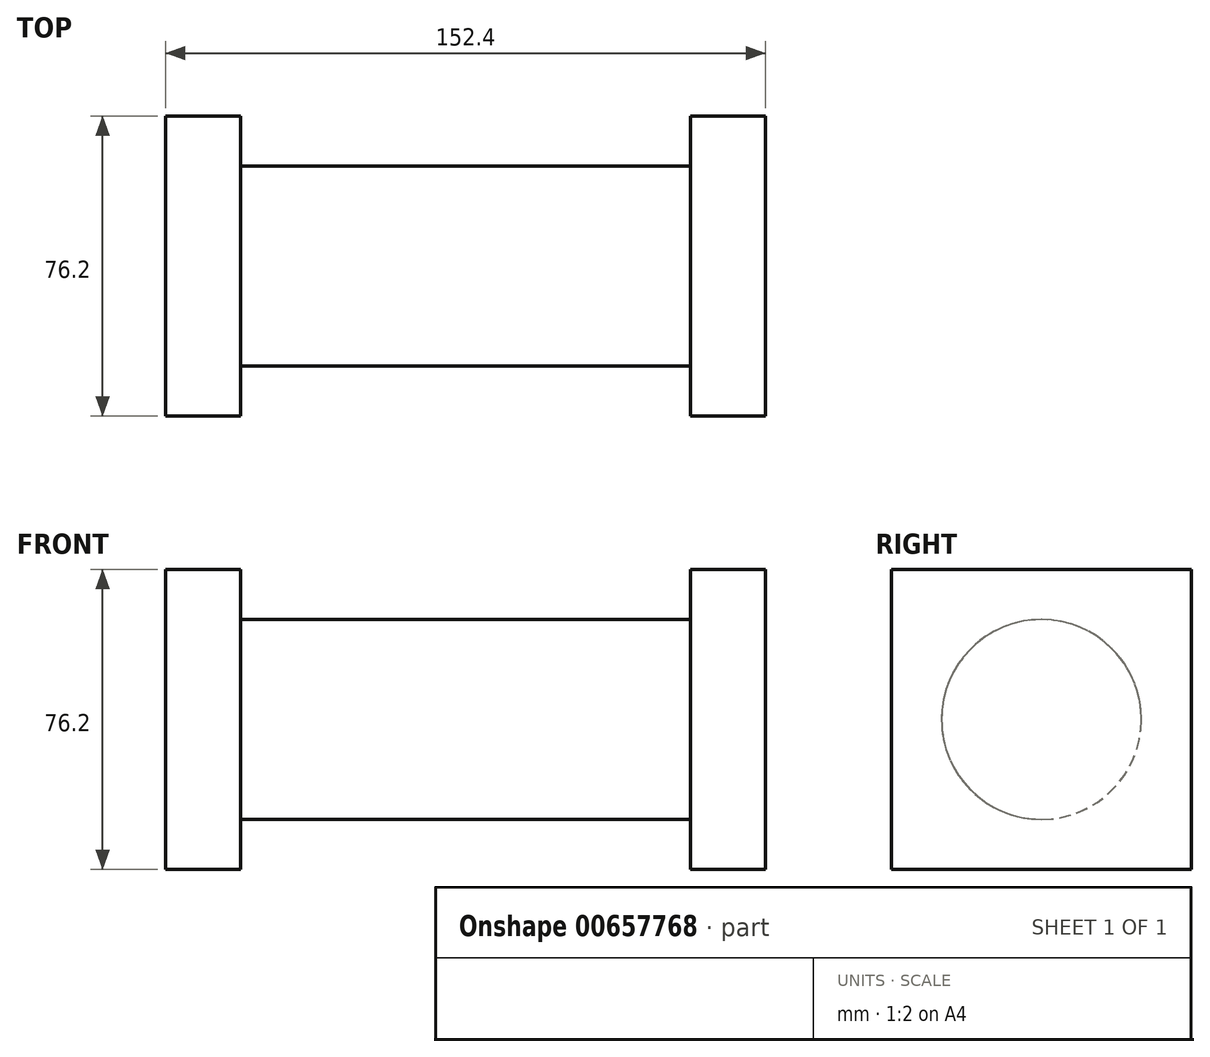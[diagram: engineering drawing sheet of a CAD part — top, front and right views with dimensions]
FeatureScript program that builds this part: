
annotation { "Feature Type Name" : "Feature", "Feature Type Description" : "" }
export const myFeature = defineFeature(function(context is Context, id is Id, definition is map)
    precondition{}
    {
        {
            var Q0;
            Q0=qCreatedBy(makeId("Right.planeOp"),FACE);
            var sketch = newSketch(context, id + "F0", { "sketchPlane" : qUnion([Q0])});
            skLineSegment(sketch, "E0.bottom", {"start": v(38.1, 38.1) * mm, "end": v(-38.1, 38.1) * mm});
            skLineSegment(sketch, "E0.top", {"start": v(38.1, -38.1) * mm, "end": v(-38.1, -38.1) * mm});
            skLineSegment(sketch, "E0.left", {"start": v(38.1, 38.1) * mm, "end": v(38.1, -38.1) * mm});
            skLineSegment(sketch, "E0.right", {"start": v(-38.1, 38.1) * mm, "end": v(-38.1, -38.1) * mm});
            skPoint(sketch, "E0.middle", {"position": v(0, 0) * mm});
            skSolve(sketch);
        }
        {
            var Q0;
            Q0=makeQuery(id+"F0.imprint","IMPRINT",FACE,{"disambiguationData":[TD([[makeQuery(id+"F0.imprint","IMPRINT",EDGE,{"derivedFrom":sQuery(id+"F0.wireOp",EDGE,"E0.bottom")}),1.0]])]});
            extrude(context, id + "F1", {"entities" : qUnion([Q0]), "depth" : 19.05 * mm, "offsetDistance" : 25.4 * mm});
        }
        {
            var Q0;
            Q0=makeQuery(id+"F1.opExtrude","SWEPT_BODY",BODY,{"disambiguationData":[OSD([sQuery(id+"F0.wireOp",EDGE,"E0.bottom"),sQuery(id+"F0.wireOp",EDGE,"E0.top"),sQuery(id+"F0.wireOp",EDGE,"E0.left"),sQuery(id+"F0.wireOp",EDGE,"E0.right")])]});
            var Q1;
            Q1=makeQuery(id+"FDAb5iPeceIPNus_1.opExtrude","SWEPT_BODY",BODY,{"disambiguationData":[OSD([sQuery(id+"FE8N3ztqaKI7V6A_1.wireOp",EDGE,"tNB3SxLx-dCB2-IcOf-TGt4-5QjExDtP5x2O")])]});
            transform(context, id + "F2", {"entities" : qUnion([Q0, Q1]), "transformType" : TransformType.TRANSLATION_3D, "dx" : -76.2 * mm, "dy" : 0 * mm, "dz" : 0 * mm, "makeCopy" : false});
        }
        {
            var Q0;
            Q0=makeQuery(id+"F1.opExtrude","SWEPT_BODY",BODY,{"disambiguationData":[OSD([sQuery(id+"F0.wireOp",EDGE,"E0.bottom"),sQuery(id+"F0.wireOp",EDGE,"E0.top"),sQuery(id+"F0.wireOp",EDGE,"E0.left"),sQuery(id+"F0.wireOp",EDGE,"E0.right")])]});
            var Q1;
            Q1=makeQuery(id+"F0.imprint","IMPRINT",FACE,{"disambiguationData":[TD([[makeQuery(id+"F0.imprint","IMPRINT",EDGE,{"derivedFrom":sQuery(id+"F0.wireOp",EDGE,"E0.bottom")}),1.0]])]});
            mirror(context, id + "F3", {"entities" : qUnion([Q0]), "mirrorPlane" : qUnion([Q1])});
        }
        {
            var Q0;
            Q0=makeQuery(id+"F3.opPattern","COPY",FACE,{"derivedFrom":makeQuery(id+"F1.opExtrude","CAP_FACE",FACE,{"disambiguationData":[OSD([sQuery(id+"F0.wireOp",EDGE,"E0.bottom"),sQuery(id+"F0.wireOp",EDGE,"E0.top"),sQuery(id+"F0.wireOp",EDGE,"E0.left"),sQuery(id+"F0.wireOp",EDGE,"E0.right")])],"isStart":true}),"instanceName":"1"});
            var sketch = newSketch(context, id + "F4", { "sketchPlane" : qUnion([Q0])});
            skCircle(sketch, "E1", {"center": v(0, 0) * mm, "radius": 25.4 * mm});
            skSolve(sketch);
        }
        {
            var Q0;
            Q0=makeQuery(id+"F4.imprint","IMPRINT",FACE,{"disambiguationData":[TD([[makeQuery(id+"F4.imprint","IMPRINT",EDGE,{"derivedFrom":sQuery(id+"F4.wireOp",EDGE,"E1")}),1.0]])]});
            extrude(context, id + "F5", {"entities" : qUnion([Q0]), "operationType" : NewBodyOperationType.ADD, "depth" : -152.4 * mm, "offsetDistance" : 25.4 * mm});
        }
    });
